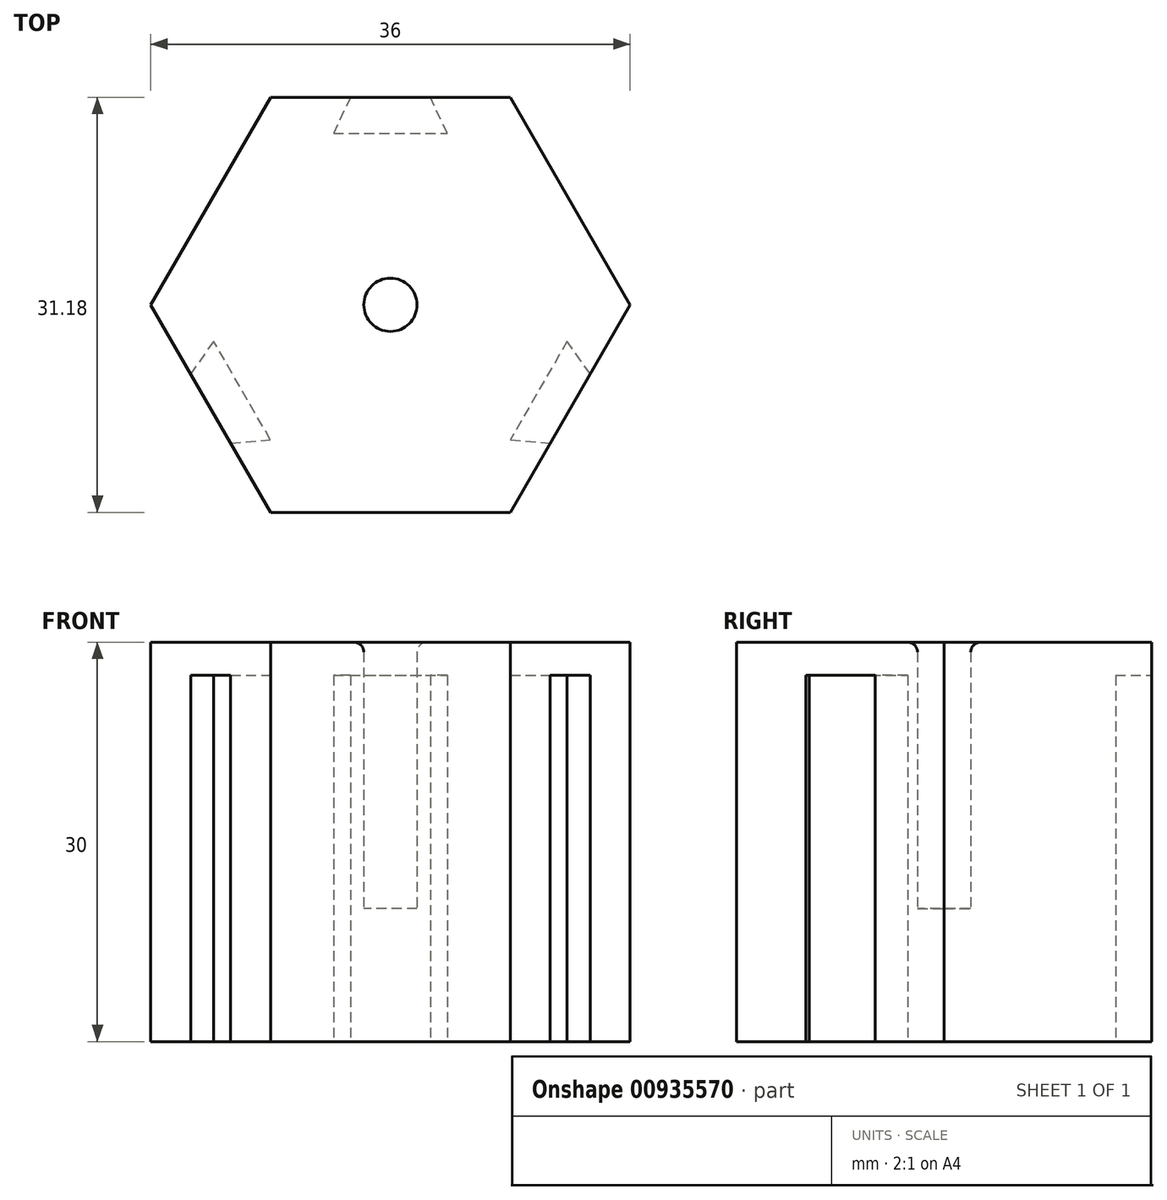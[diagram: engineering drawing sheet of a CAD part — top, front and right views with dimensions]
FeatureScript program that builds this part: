
annotation { "Feature Type Name" : "Feature", "Feature Type Description" : "" }
export const myFeature = defineFeature(function(context is Context, id is Id, definition is map)
    precondition{}
    {
        {
            var Q0;
            Q0=qCreatedBy(makeId("Top.planeOp"),FACE);
            var sketch = newSketch(context, id + "F0", { "sketchPlane" : qUnion([Q0])});
            skCircle(sketch, "E0.cCircle", {"center": v(0, 0) * mm, "radius": 18 * mm, "construction": true});
            skLineSegment(sketch, "E0.0", {"start": v(-9, 15.59) * mm, "end": v(-3, 15.59) * mm});
            skLineSegment(sketch, "E0.1", {"start": v(9, 15.59) * mm, "end": v(18, 0) * mm});
            skLineSegment(sketch, "E0.2", {"start": v(18, 0) * mm, "end": v(15, -5.2) * mm});
            skLineSegment(sketch, "E0.3", {"start": v(9, -15.59) * mm, "end": v(-9, -15.59) * mm});
            skLineSegment(sketch, "E0.4", {"start": v(-9, -15.59) * mm, "end": v(-12, -10.4) * mm});
            skLineSegment(sketch, "E0.5", {"start": v(-18, 0) * mm, "end": v(-9, 15.59) * mm});
            skCircle(sketch, "E1", {"center": v(0, 0) * mm, "radius": 2 * mm});
            skLineSegment(sketch, "E2", {"start": v(-3, 15.59) * mm, "end": v(-4.27, 12.87) * mm});
            skLineSegment(sketch, "E3", {"start": v(-4.27, 12.87) * mm, "end": v(4.27, 12.87) * mm});
            skLineSegment(sketch, "E4", {"start": v(4.27, 12.87) * mm, "end": v(3, 15.59) * mm});
            skLineSegment(sketch, "E5.1.0", {"start": v(-12, -10.4) * mm, "end": v(-9.01, -10.13) * mm});
            skLineSegment(sketch, "E5.1.1", {"start": v(-9.01, -10.13) * mm, "end": v(-13.28, -2.74) * mm});
            skLineSegment(sketch, "E5.1.2", {"start": v(-13.28, -2.74) * mm, "end": v(-15, -5.2) * mm});
            skLineSegment(sketch, "E5.2.0", {"start": v(15, -5.2) * mm, "end": v(13.28, -2.74) * mm});
            skLineSegment(sketch, "E5.2.1", {"start": v(13.28, -2.74) * mm, "end": v(9.01, -10.13) * mm});
            skLineSegment(sketch, "E5.2.2", {"start": v(9.01, -10.13) * mm, "end": v(12, -10.4) * mm});
            skLineSegment(sketch, "E6.trimOffspring", {"start": v(3, 15.59) * mm, "end": v(9, 15.59) * mm});
            skLineSegment(sketch, "E7.trimOffspring", {"start": v(-15, -5.2) * mm, "end": v(-18, 0) * mm});
            skLineSegment(sketch, "E8.trimOffspring", {"start": v(12, -10.4) * mm, "end": v(9, -15.59) * mm});
            skLineSegment(sketch, "E9", {"start": v(-15, -5.2) * mm, "end": v(-12, -10.4) * mm});
            skLineSegment(sketch, "E10", {"start": v(15, -5.2) * mm, "end": v(12, -10.4) * mm});
            skLineSegment(sketch, "E11", {"start": v(-3, 15.59) * mm, "end": v(3, 15.59) * mm});
            skSolve(sketch);
        }
        {
            var Q0;
            Q0=makeQuery(id+"F0.imprint","IMPRINT",FACE,{"disambiguationData":[TD([[makeQuery(id+"F0.imprint","IMPRINT",EDGE,{"derivedFrom":sQuery(id+"F0.wireOp",EDGE,"E1")}),1.0]])]});
            extrude(context, id + "F1", {"entities" : qUnion([Q0]), "depth" : 10 * mm, "offsetDistance" : 25 * mm});
        }
        {
            var Q0;
            Q0=makeQuery(id+"F0.imprint","IMPRINT",FACE,{"disambiguationData":[TD([[makeQuery(id+"F0.imprint","IMPRINT",EDGE,{"derivedFrom":sQuery(id+"F0.wireOp",EDGE,"E0.0")}),-1.0]])]});
            extrude(context, id + "F2", {"entities" : qUnion([Q0]), "operationType" : NewBodyOperationType.ADD, "depth" : 30 * mm, "offsetDistance" : 25 * mm});
        }
        {
            var Q0;
            Q0=makeQuery(id+"F0.imprint","IMPRINT",FACE,{"disambiguationData":[TD([[makeQuery(id+"F0.imprint","IMPRINT",EDGE,{"derivedFrom":sQuery(id+"F0.wireOp",EDGE,"E2")}),1.0]])]});
            var Q1;
            Q1=makeQuery(id+"F0.imprint","IMPRINT",FACE,{"disambiguationData":[TD([[makeQuery(id+"F0.imprint","IMPRINT",EDGE,{"derivedFrom":sQuery(id+"F0.wireOp",EDGE,"E5.1.0")}),1.0]])]});
            var Q2;
            Q2=makeQuery(id+"F0.imprint","IMPRINT",FACE,{"disambiguationData":[TD([[makeQuery(id+"F0.imprint","IMPRINT",EDGE,{"derivedFrom":sQuery(id+"F0.wireOp",EDGE,"E5.2.0")}),1.0]])]});
            extrude(context, id + "F3", {"entities" : qUnion([Q0, Q1, Q2]), "operationType" : NewBodyOperationType.ADD, "depth" : 30 * mm, "offsetDistance" : 25 * mm, "hasSecondDirection" : true, "secondDirectionOppositeDirection" : true, "secondDirectionDepth" : -27.5 * mm});
        }
        {
            var Q0;
            Q0=makeQuery(id+"F2.opExtrude","CAP_EDGE",EDGE,{"disambiguationData":[OSD([sQuery(id+"F0.wireOp",EDGE,"E1")])],"isStart":false});
            fillet(context, id + "F4", {"entities" : qUnion([Q0]), "radius" : .75 * mm, "tangentPropagation" : true, "allowEdgeOverflow" : false});
        }
    });
